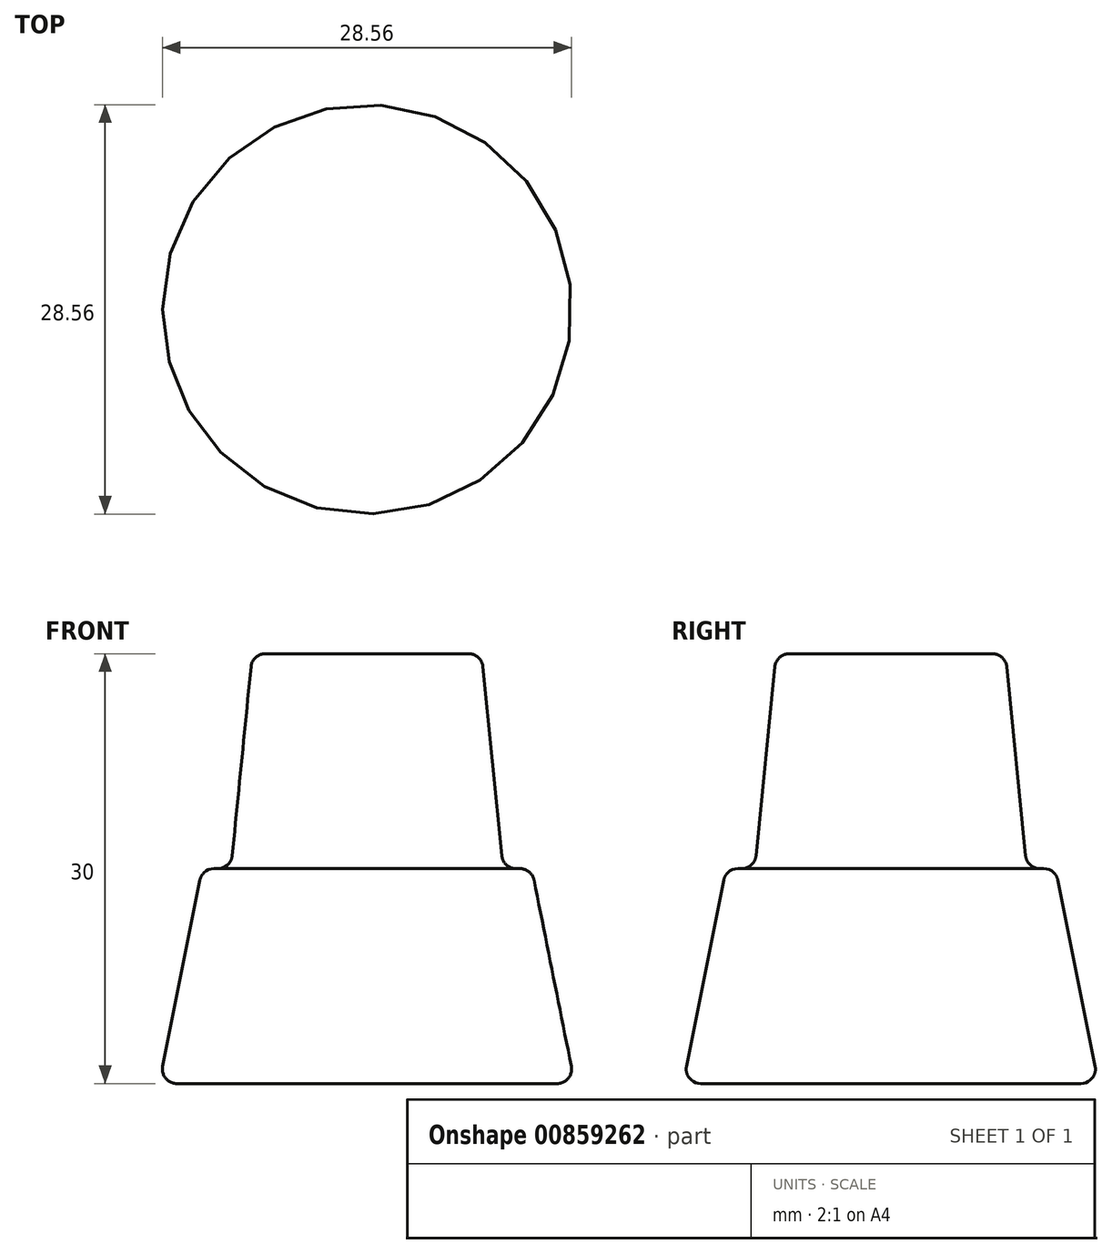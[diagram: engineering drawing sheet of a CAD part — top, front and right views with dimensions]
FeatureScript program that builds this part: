
annotation { "Feature Type Name" : "Feature", "Feature Type Description" : "" }
export const myFeature = defineFeature(function(context is Context, id is Id, definition is map)
    precondition{}
    {
        {
            var Q0;
            Q0=qCreatedBy(makeId("Front.planeOp"),FACE);
            var sketch = newSketch(context, id + "F0", { "sketchPlane" : qUnion([Q0])});
            skLineSegment(sketch, "E0", {"start": v(0, 15) * mm, "end": v(0, 0) * mm});
            skLineSegment(sketch, "E1", {"start": v(9.5, 15) * mm, "end": v(11.5, 15) * mm});
            skLineSegment(sketch, "E2", {"start": v(11.5, 15) * mm, "end": v(14.5, 0) * mm});
            skLineSegment(sketch, "E3", {"start": v(14.5, 0) * mm, "end": v(0, 0) * mm});
            skLineSegment(sketch, "E4", {"start": v(0, 15) * mm, "end": v(0, 30) * mm});
            skLineSegment(sketch, "E5", {"start": v(0, 30) * mm, "end": v(8, 30) * mm});
            skLineSegment(sketch, "E6", {"start": v(8, 30) * mm, "end": v(9.5, 15) * mm});
            skSolve(sketch);
        }
        {
            var Q0;
            Q0=makeQuery(id+"F0.imprint","IMPRINT",FACE,{"disambiguationData":[TD([[makeQuery(id+"F0.imprint","IMPRINT",EDGE,{"derivedFrom":sQuery(id+"F0.wireOp",EDGE,"E0")}),1.0]])]});
            var Q1;
            Q1=sQuery(id+"F0.wireOp",EDGE,"E0");
            revolve(context, id + "F1", {"surfaceOperationType" : NewSurfaceOperationType.NEW, "entities" : qUnion([Q0]), "axis" : qUnion([Q1]), "revolveType" : RevolveType.FULL});
        }
        {
            var Q0;
            Q0=makeQuery(id+"F1.opRevolve","SWEPT_EDGE",EDGE,{"disambiguationData":[OSD([sQuery(id+"F0.wireOp",EDGE,"E1"),sQuery(id+"F0.wireOp",EDGE,"E2")])]});
            var Q1;
            Q1=makeQuery(id+"F1.opRevolve","SWEPT_EDGE",EDGE,{"disambiguationData":[OSD([sQuery(id+"F0.wireOp",EDGE,"E1"),sQuery(id+"F0.wireOp",EDGE,"E6")])]});
            var Q2;
            Q2=makeQuery(id+"F1.opRevolve","SWEPT_EDGE",EDGE,{"disambiguationData":[OSD([sQuery(id+"F0.wireOp",EDGE,"E5"),sQuery(id+"F0.wireOp",EDGE,"E6")])]});
            var Q3;
            Q3=makeQuery(id+"F1.opRevolve","SWEPT_EDGE",EDGE,{"disambiguationData":[OSD([sQuery(id+"F0.wireOp",EDGE,"E2"),sQuery(id+"F0.wireOp",EDGE,"E3")])]});
            fillet(context, id + "F2", {"entities" : qUnion([Q0, Q1, Q2, Q3]), "radius" : 1 * mm, "tangentPropagation" : true, "allowEdgeOverflow" : false});
        }
    });
